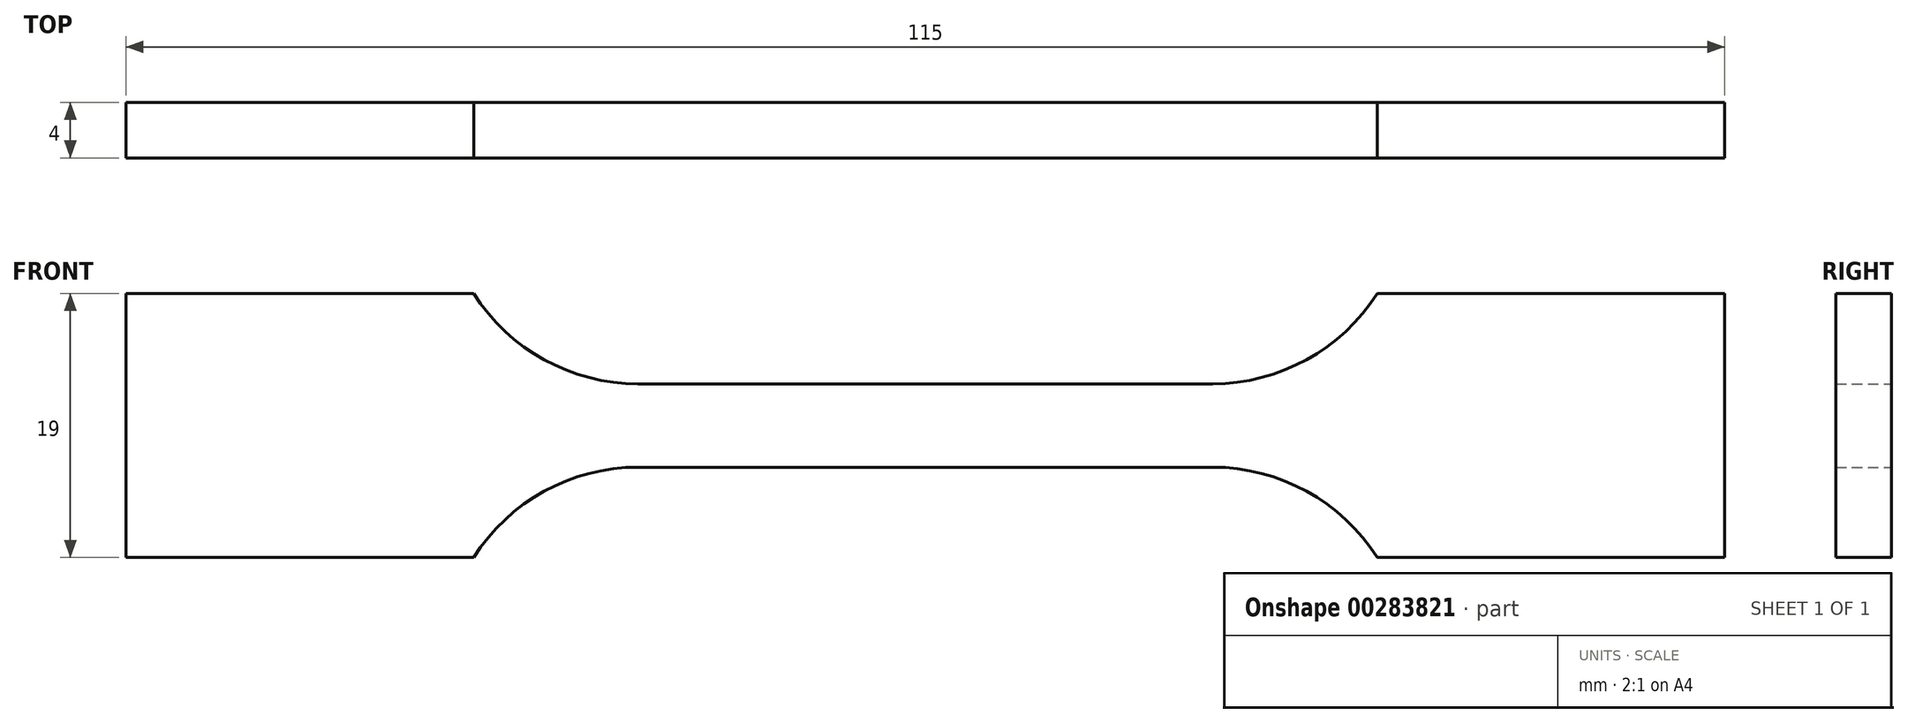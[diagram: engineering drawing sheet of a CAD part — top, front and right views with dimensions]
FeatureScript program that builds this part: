
annotation { "Feature Type Name" : "Feature", "Feature Type Description" : "" }
export const myFeature = defineFeature(function(context is Context, id is Id, definition is map)
    precondition{}
    {
        {
            var Q0;
            Q0=qCreatedBy(makeId("Front.planeOp"),FACE);
            var sketch = newSketch(context, id + "F0", { "sketchPlane" : qUnion([Q0])});
            skLineSegment(sketch, "E0", {"start": v(0, 3) * mm, "end": v(20.68, 3) * mm});
            skArc(sketch, "E1", {"start": v(20.68, 3) * mm, "mid": v(27.42, 4.73) * mm, "end": v(32.5, 9.5) * mm});
            skLineSegment(sketch, "E2", {"start": v(32.5, 9.5) * mm, "end": v(57.5, 9.5) * mm});
            skArc(sketch, "E3.MirrorCS", {"start": v(20.68, -3) * mm, "mid": v(27.42, -4.73) * mm, "end": v(32.5, -9.5) * mm});
            skLineSegment(sketch, "E4.MirrorCS", {"start": v(32.5, -9.5) * mm, "end": v(57.5, -9.5) * mm});
            skLineSegment(sketch, "E5.MirrorCS", {"start": v(0, -3) * mm, "end": v(20.68, -3) * mm});
            skArc(sketch, "E6.MirrorCS", {"start": v(-20.68, -3) * mm, "mid": v(-27.42, -4.73) * mm, "end": v(-32.5, -9.5) * mm});
            skLineSegment(sketch, "E7.MirrorCS", {"start": v(-32.5, -9.5) * mm, "end": v(-57.5, -9.5) * mm});
            skLineSegment(sketch, "E8.MirrorCS", {"start": v(-32.5, 9.5) * mm, "end": v(-57.5, 9.5) * mm});
            skLineSegment(sketch, "E9.MirrorCS", {"start": v(0, 3) * mm, "end": v(-20.68, 3) * mm});
            skLineSegment(sketch, "E10.MirrorCS", {"start": v(0, -3) * mm, "end": v(-20.68, -3) * mm});
            skArc(sketch, "E11.MirrorCS", {"start": v(-20.68, 3) * mm, "mid": v(-27.42, 4.73) * mm, "end": v(-32.5, 9.5) * mm});
            skLineSegment(sketch, "E12", {"start": v(-57.5, 9.5) * mm, "end": v(-57.5, -9.5) * mm});
            skLineSegment(sketch, "E13", {"start": v(57.5, 9.5) * mm, "end": v(57.5, -9.5) * mm});
            skSolve(sketch);
        }
        {
            var Q0;
            Q0 = qSketchRegion(id + "F0", true);
            extrude(context, id + "F1", {"entities" : qUnion([Q0]), "endBound" : BoundingType.SYMMETRIC, "depth" : 4 * mm});
        }
    });
